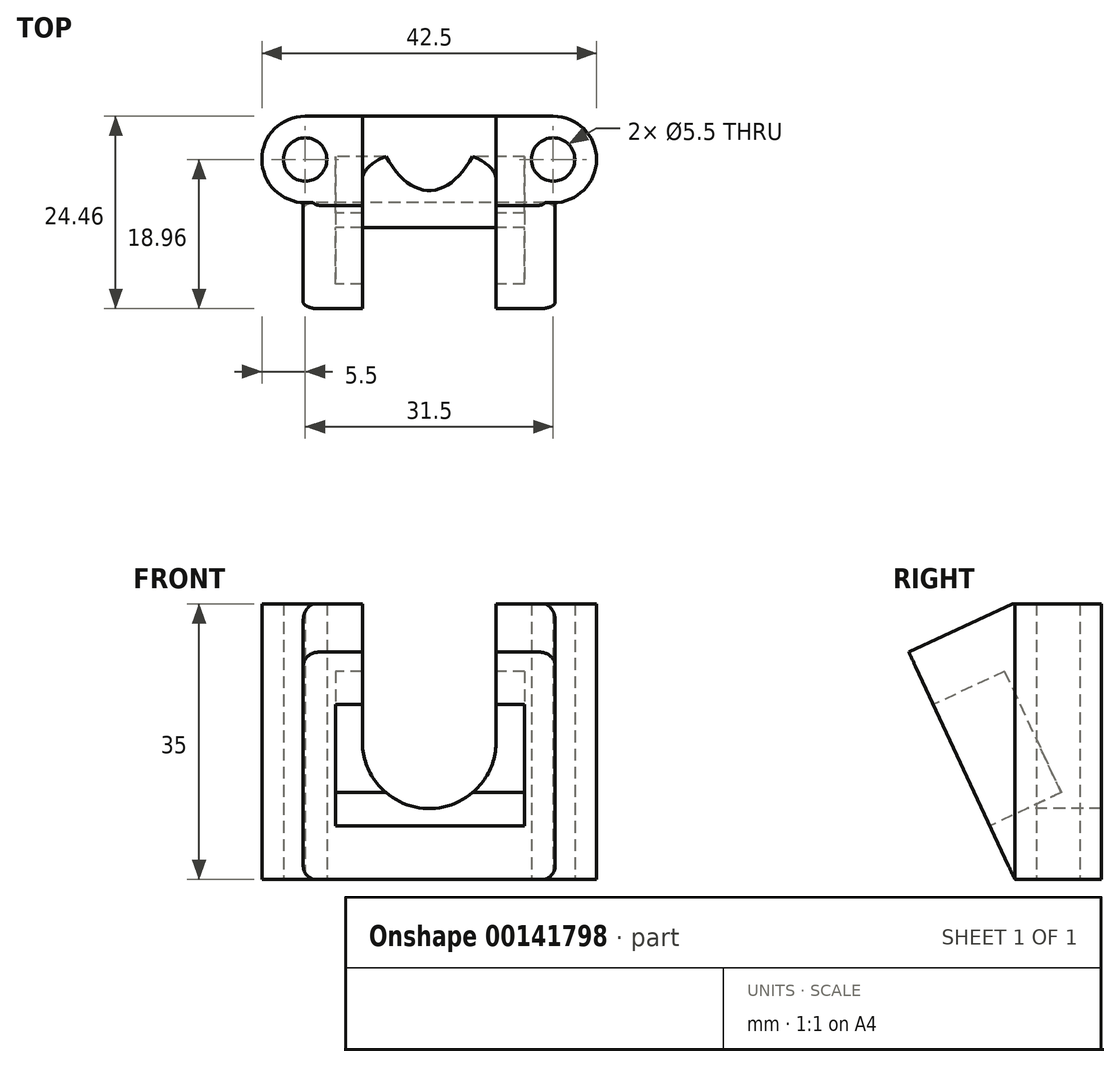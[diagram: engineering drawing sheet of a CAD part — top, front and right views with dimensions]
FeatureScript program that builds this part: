
annotation { "Feature Type Name" : "Feature", "Feature Type Description" : "" }
export const myFeature = defineFeature(function(context is Context, id is Id, definition is map)
    precondition{}
    {
        {
            var Q0;
            Q0=qCreatedBy(makeId("Top.planeOp"),FACE);
            var sketch = newSketch(context, id + "F0", { "sketchPlane" : qUnion([Q0])});
            skLineSegment(sketch, "E0", {"start": v(-18.5, 0) * mm, "end": v(18.5, 0) * mm, "construction": true});
            skCircle(sketch, "E1", {"center": v(-15.75, 0) * mm, "radius": 2.75 * mm});
            skCircle(sketch, "E2", {"center": v(15.75, 0) * mm, "radius": 2.75 * mm});
            skArc(sketch, "E3", {"start": v(-15.75, 5.5) * mm, "mid": v(-21.25, 0) * mm, "end": v(-15.75, -5.5) * mm});
            skArc(sketch, "E4", {"start": v(15.75, -5.5) * mm, "mid": v(21.25, 0) * mm, "end": v(15.75, 5.5) * mm});
            skLineSegment(sketch, "E5", {"start": v(-15.75, 5.5) * mm, "end": v(15.75, 5.5) * mm});
            skLineSegment(sketch, "E6", {"start": v(-15.75, -5.5) * mm, "end": v(15.75, -5.5) * mm});
            skSolve(sketch);
        }
        {
            var Q0;
            Q0=makeQuery(id+"F0.imprint","IMPRINT",FACE,{"disambiguationData":[TD([[makeQuery(id+"F0.imprint","IMPRINT",EDGE,{"derivedFrom":sQuery(id+"F0.wireOp",EDGE,"E1")}),-1.0]])]});
            extrude(context, id + "F1", {"entities" : qUnion([Q0]), "depth" : 35 * mm});
        }
        {
            var Q0;
            Q0=makeQuery(id+"F1.opExtrude","SWEPT_FACE",FACE,{"disambiguationData":[OSD([sQuery(id+"F0.wireOp",EDGE,"E6")])]});
            var sketch = newSketch(context, id + "F2", { "sketchPlane" : qUnion([Q0])});
            skLineSegment(sketch, "E7", {"start": v(-15.75, 35) * mm, "end": v(15.75, 0) * mm, "construction": true});
            skArc(sketch, "E8", {"start": v(-8.5, 17.5) * mm, "mid": v(0, 9) * mm, "end": v(8.5, 17.5) * mm});
            skLineSegment(sketch, "E9", {"start": v(-8.5, 17.5) * mm, "end": v(-8.5, 35) * mm});
            skLineSegment(sketch, "E10", {"start": v(8.5, 17.5) * mm, "end": v(8.5, 35) * mm});
            skLineSegment(sketch, "E11", {"start": v(8.5, 35) * mm, "end": v(-8.5, 35) * mm});
            skSolve(sketch);
        }
        {
            var Q0;
            Q0=qSketchRegion(id+"F2",true);
            extrude(context, id + "F3", {"entities" : qUnion([Q0]), "operationType" : NewBodyOperationType.REMOVE, "endBound" : BoundingType.THROUGH_ALL, "oppositeDirection" : true, "depth" : 25 * mm});
        }
        {
            var Q0;
            Q0=makeQuery(id+"F1.opExtrude","CAP_EDGE",EDGE,{"disambiguationData":[OSD([sQuery(id+"F0.wireOp",EDGE,"E6")])],"isStart":true});
            cPlane(context, id + "F4", {"entities" : qUnion([Q0]), "cplaneType" : CPlaneType.LINE_ANGLE, "offset" : 150 * mm, "angle" : 25 * degree, "width" : 150 * mm, "height" : 150 * mm});
        }
        {
            var Q0;
            Q0=qCreatedBy(id+"F4.planeOp",FACE);
            var sketch = newSketch(context, id + "F5", { "sketchPlane" : qUnion([Q0])});
            skPoint(sketch, "E12.0", {"position": v(15.75, 2.32) * mm});
            skPoint(sketch, "E13.0", {"position": v(-15.75, 34.05) * mm});
            skLineSegment(sketch, "E14", {"start": v(-15.75, 34.05) * mm, "end": v(15.75, 2.32) * mm, "construction": true});
            skLineSegment(sketch, "E15.rect.bottom", {"start": v(14, 32.18) * mm, "end": v(-14, 32.18) * mm, "construction": true});
            skLineSegment(sketch, "E15.rect.top", {"start": v(14, 4.18) * mm, "end": v(-14, 4.18) * mm, "construction": true});
            skLineSegment(sketch, "E15.rect.left", {"start": v(14, 32.18) * mm, "end": v(14, 4.18) * mm, "construction": true});
            skLineSegment(sketch, "E15.rect.right", {"start": v(-14, 32.18) * mm, "end": v(-14, 4.18) * mm, "construction": true});
            skPoint(sketch, "E15.rect.middle", {"position": v(0, 18.18) * mm});
            skLineSegment(sketch, "E16.0", {"start": v(14, 34.18) * mm, "end": v(-14, 34.18) * mm});
            skLineSegment(sketch, "E16.1", {"start": v(16, 32.18) * mm, "end": v(16, 4.18) * mm});
            skLineSegment(sketch, "E16.2", {"start": v(14, 2.18) * mm, "end": v(-14, 2.18) * mm});
            skLineSegment(sketch, "E16.3", {"start": v(-16, 32.18) * mm, "end": v(-16, 4.18) * mm});
            skPoint(sketch, "E17.visualSharp", {"position": v(16, 34.18) * mm});
            skArc(sketch, "E17.filletArc", {"start": v(16, 32.18) * mm, "mid": v(15.41, 33.6) * mm, "end": v(14, 34.18) * mm});
            skPoint(sketch, "E18.visualSharp", {"position": v(16, 2.18) * mm});
            skArc(sketch, "E18.filletArc", {"start": v(14, 2.18) * mm, "mid": v(15.41, 2.77) * mm, "end": v(16, 4.18) * mm});
            skPoint(sketch, "E19.visualSharp", {"position": v(-16, 2.18) * mm});
            skArc(sketch, "E19.filletArc", {"start": v(-16, 4.18) * mm, "mid": v(-15.41, 2.77) * mm, "end": v(-14, 2.18) * mm});
            skPoint(sketch, "E20.visualSharp", {"position": v(-16, 34.18) * mm});
            skArc(sketch, "E20.filletArc", {"start": v(-14, 34.18) * mm, "mid": v(-15.41, 33.6) * mm, "end": v(-16, 32.18) * mm});
            skSolve(sketch);
        }
        {
            var Q0;
            Q0=makeQuery(id+"F5.imprint","IMPRINT",FACE,{"disambiguationData":[TD([[makeQuery(id+"F5.imprint","IMPRINT",EDGE,{"derivedFrom":sQuery(id+"F5.wireOp",EDGE,"E16.0")}),1.0]])]});
            var Q1;
            Q1=makeQuery(id+"F1.opExtrude","SWEPT_FACE",FACE,{"disambiguationData":[OSD([sQuery(id+"F0.wireOp",EDGE,"E6")])]});
            extrude(context, id + "F6", {"entities" : qUnion([Q0]), "operationType" : NewBodyOperationType.ADD, "endBound" : BoundingType.UP_TO_SURFACE, "endBoundEntityFace" : qUnion([Q1]), "depth" : 25 * mm});
        }
        {
            var Q0;
            Q0=makeQuery(id+"F1.opExtrude","SWEPT_FACE",FACE,{"disambiguationData":[OSD([sQuery(id+"F0.wireOp",EDGE,"E5")])]});
            var sketch = newSketch(context, id + "F7", { "sketchPlane" : qUnion([Q0])});
            skLineSegment(sketch, "E21.0", {"start": v(-8.5, 35) * mm, "end": v(-8.5, 17.5) * mm});
            skLineSegment(sketch, "E22.0", {"start": v(8.5, 35) * mm, "end": v(8.5, 17.5) * mm});
            skArc(sketch, "E23.0", {"start": v(-8.5, 17.5) * mm, "mid": v(0, 9) * mm, "end": v(8.5, 17.5) * mm});
            skLineSegment(sketch, "E24", {"start": v(-8.5, 35) * mm, "end": v(8.5, 35) * mm});
            skLineSegment(sketch, "E25.bottom", {"start": v(15.75, 35) * mm, "end": v(-15.75, 35) * mm});
            skLineSegment(sketch, "E25.top", {"start": v(15.75, 35.6) * mm, "end": v(-15.75, 35.6) * mm});
            skLineSegment(sketch, "E25.left", {"start": v(15.75, 35) * mm, "end": v(15.75, 35.6) * mm});
            skLineSegment(sketch, "E25.right", {"start": v(-15.75, 35) * mm, "end": v(-15.75, 35.6) * mm});
            skSolve(sketch);
        }
        {
            var Q0;
            Q0=qSketchRegion(id+"F7",true);
            extrude(context, id + "F8", {"entities" : qUnion([Q0]), "operationType" : NewBodyOperationType.REMOVE, "oppositeDirection" : true, "depth" : 25 * mm});
        }
        {
            var Q0;
            Q0=makeQuery(id+"F6.opExtrude","CAP_FACE",FACE,{"disambiguationData":[OSD([sQuery(id+"F5.wireOp",EDGE,"E16.0"),sQuery(id+"F5.wireOp",EDGE,"E16.1"),sQuery(id+"F5.wireOp",EDGE,"E16.2"),sQuery(id+"F5.wireOp",EDGE,"E16.3"),sQuery(id+"F5.wireOp",EDGE,"E17.filletArc"),sQuery(id+"F5.wireOp",EDGE,"E18.filletArc"),sQuery(id+"F5.wireOp",EDGE,"E19.filletArc"),sQuery(id+"F5.wireOp",EDGE,"E20.filletArc")])],"isStart":true});
            var sketch = newSketch(context, id + "F9", { "sketchPlane" : qUnion([Q0])});
            skLineSegment(sketch, "E26.rect.bottom", {"start": v(12.12, 26.83) * mm, "end": v(-11.88, 26.83) * mm});
            skLineSegment(sketch, "E26.rect.top", {"start": v(12.12, 9.83) * mm, "end": v(-11.88, 9.83) * mm});
            skLineSegment(sketch, "E26.rect.left", {"start": v(12.12, 26.83) * mm, "end": v(12.12, 9.83) * mm});
            skLineSegment(sketch, "E26.rect.right", {"start": v(-11.88, 26.83) * mm, "end": v(-11.88, 9.83) * mm});
            skPoint(sketch, "E26.rect.middle", {"position": v(0.12, 18.33) * mm});
            skLineSegment(sketch, "E27", {"start": v(-15.41, 33.6) * mm, "end": v(15.65, 3.06) * mm, "construction": true});
            skSolve(sketch);
        }
        {
            var Q0;
            {var subQ1=makeQuery(id+"F6.opExtrude","CAP_FACE",FACE,{"disambiguationData":[OSD([sQuery(id+"F5.wireOp",EDGE,"E16.0"),sQuery(id+"F5.wireOp",EDGE,"E16.1"),sQuery(id+"F5.wireOp",EDGE,"E16.2"),sQuery(id+"F5.wireOp",EDGE,"E16.3"),sQuery(id+"F5.wireOp",EDGE,"E17.filletArc"),sQuery(id+"F5.wireOp",EDGE,"E18.filletArc"),sQuery(id+"F5.wireOp",EDGE,"E19.filletArc"),sQuery(id+"F5.wireOp",EDGE,"E20.filletArc")])],"isStart":true});var subQ6=makeQuery(id+"F8.boolean.opBoolean","INTERSECT",EDGE,{"derivedFrom":[subQ1,makeQuery(id+"F8.opExtrude","SWEPT_FACE",FACE,{"disambiguationData":[OSD([sQuery(id+"F7.wireOp",EDGE,"E23.0")])]})]});Q0=makeQuery(id+"F9.imprint","IMPRINT",FACE,{"disambiguationData":[TD([[makeQuery(id+"F9.imprint","IMPRINT",EDGE,{"derivedFrom":subQ6}),-1.0]])]});}
            var Q1;
            Q1=makeQuery(id+"F9.imprint","IMPRINT",FACE,{"disambiguationData":[TD([[makeQuery(id+"F9.imprint","IMPRINT",EDGE,{"derivedFrom":sQuery(id+"F9.wireOp",EDGE,"E26.rect.top")}),-1.0]])]});
            extrude(context, id + "F10", {"entities" : qUnion([Q0, Q1]), "operationType" : NewBodyOperationType.REMOVE, "oppositeDirection" : true, "depth" : 10 * mm});
        }
    });
